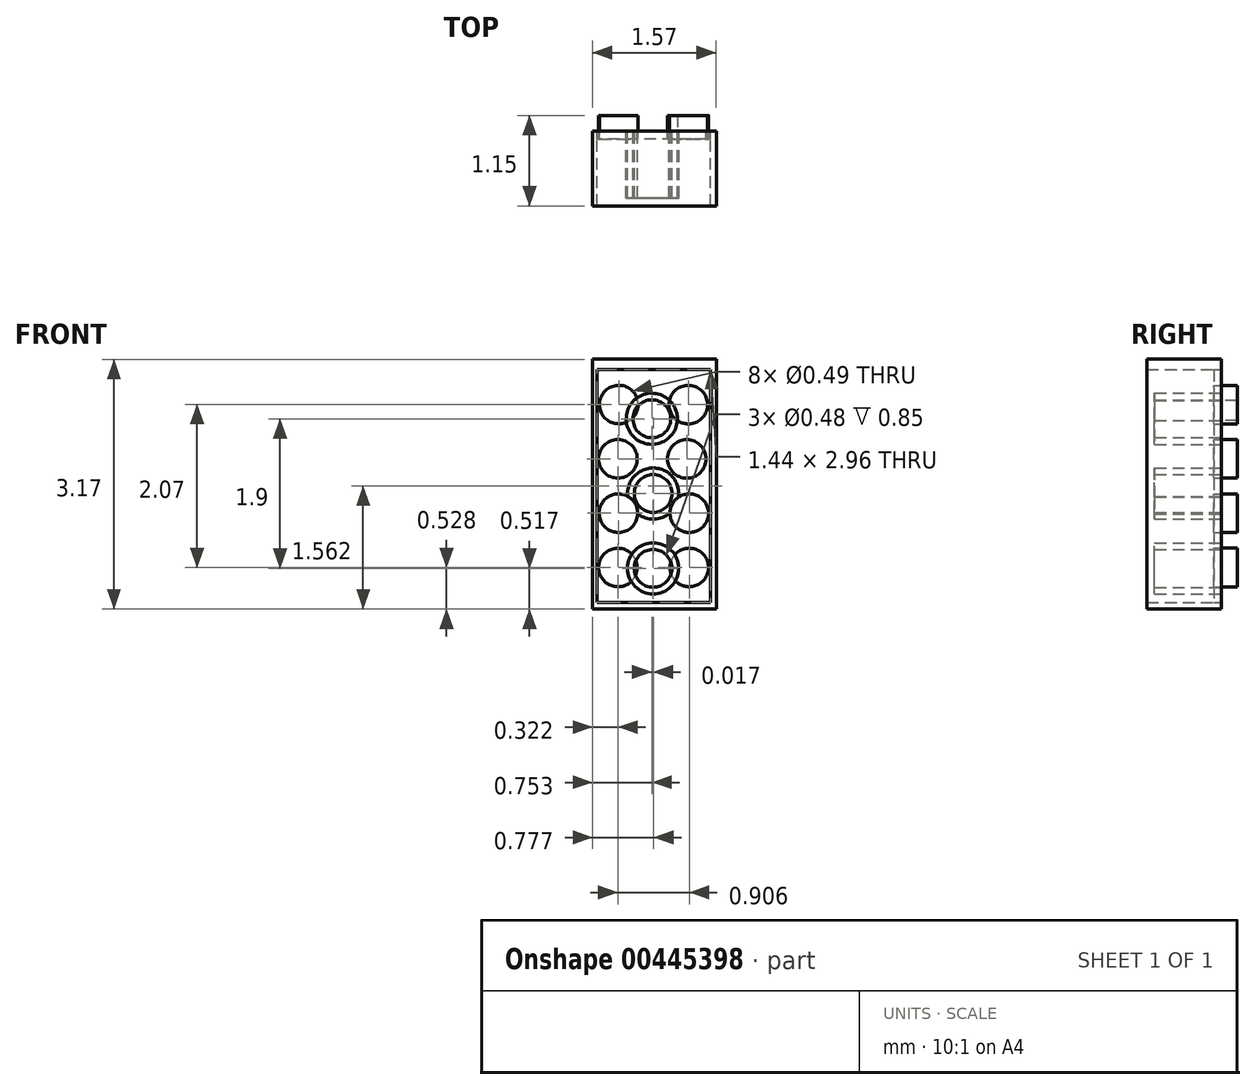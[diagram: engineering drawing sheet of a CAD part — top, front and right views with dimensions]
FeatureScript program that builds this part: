
annotation { "Feature Type Name" : "Feature", "Feature Type Description" : "" }
export const myFeature = defineFeature(function(context is Context, id is Id, definition is map)
    precondition{}
    {
        {
            var Q0;
            Q0=qCreatedBy(makeId("Front.planeOp"),FACE);
            var sketch = newSketch(context, id + "F0", { "sketchPlane" : qUnion([Q0])});
            skLineSegment(sketch, "E0.bottom", {"start": v(-2.81, -5.22) * mm, "end": v(-1.24, -5.22) * mm});
            skLineSegment(sketch, "E0.top", {"start": v(-2.81, -8.4) * mm, "end": v(-1.24, -8.4) * mm});
            skLineSegment(sketch, "E0.left", {"start": v(-2.81, -5.22) * mm, "end": v(-2.81, -8.4) * mm});
            skLineSegment(sketch, "E0.right", {"start": v(-1.24, -5.22) * mm, "end": v(-1.24, -8.4) * mm});
            skLineSegment(sketch, "E1", {"start": v(-2.75, -5.22) * mm, "end": v(-2.75, -8.4) * mm});
            skLineSegment(sketch, "E2", {"start": v(-2.75, -8.4) * mm, "end": v(-2.81, -8.3) * mm});
            skLineSegment(sketch, "E3", {"start": v(-2.81, -8.3) * mm, "end": v(-1.24, -8.3) * mm});
            skLineSegment(sketch, "E4", {"start": v(-1.24, -8.3) * mm, "end": v(-1.31, -8.4) * mm});
            skLineSegment(sketch, "E5", {"start": v(-1.31, -8.4) * mm, "end": v(-1.31, -5.22) * mm});
            skLineSegment(sketch, "E6", {"start": v(-1.31, -5.22) * mm, "end": v(-1.24, -5.35) * mm});
            skLineSegment(sketch, "E7", {"start": v(-1.24, -5.35) * mm, "end": v(-2.81, -5.35) * mm});
            skCircle(sketch, "E8", {"center": v(-2.48, -5.8) * mm, "radius": 0.24 * mm});
            skCircle(sketch, "E9", {"center": v(-1.6, -5.8) * mm, "radius": 0.24 * mm});
            skCircle(sketch, "E10", {"center": v(-2.49, -6.48) * mm, "radius": 0.24 * mm});
            skCircle(sketch, "E11", {"center": v(-1.61, -6.48) * mm, "radius": 0.24 * mm});
            skCircle(sketch, "E12", {"center": v(-2.48, -7.17) * mm, "radius": 0.24 * mm});
            skCircle(sketch, "E13", {"center": v(-1.58, -7.17) * mm, "radius": 0.24 * mm});
            skCircle(sketch, "E14", {"center": v(-1.58, -7.86) * mm, "radius": 0.24 * mm});
            skCircle(sketch, "E15", {"center": v(-2.49, -7.86) * mm, "radius": 0.24 * mm});
            skSolve(sketch);
        }
        {
            var Q0;
            Q0=makeQuery(id+"F0.imprint","IMPRINT",FACE,{"disambiguationData":[TD([[makeQuery(id+"F0.imprint","IMPRINT",EDGE,{"derivedFrom":sQuery(id+"F0.wireOp",EDGE,"E8")}),-1.0]])]});
            var sketch = newSketch(context, id + "F1", { "sketchPlane" : qUnion([Q0])});
            skCircle(sketch, "E16", {"center": v(-2.06, -5.97) * mm, "radius": 0.33 * mm});
            skCircle(sketch, "E17", {"center": v(-2.04, -6.92) * mm, "radius": 0.33 * mm});
            skCircle(sketch, "E18", {"center": v(-2.04, -7.87) * mm, "radius": 0.33 * mm});
            skCircle(sketch, "E19", {"center": v(-2.06, -5.97) * mm, "radius": 0.24 * mm});
            skCircle(sketch, "E20", {"center": v(-2.04, -6.92) * mm, "radius": 0.24 * mm});
            skCircle(sketch, "E21", {"center": v(-2.04, -7.87) * mm, "radius": 0.24 * mm});
            skSolve(sketch);
        }
        {
            var Q0;
            {var subQ0=sQuery(id+"F0.wireOp",EDGE,"E1");var subQ1=sQuery(id+"F0.wireOp",EDGE,"E0.bottom");var subQ2=makeQuery(id+"F0.imprint","INTERSECT",VERTEX,{"derivedFrom":[subQ1,subQ0]});Q0=makeQuery(id+"F0.imprint","IMPRINT",FACE,{"disambiguationData":[TD([[makeQuery(id+"F0.imprint","IMPRINT",EDGE,{"disambiguationData":[TD([[subQ2,-1.0]])],"derivedFrom":subQ0}),1.0]])]});}
            var Q1;
            {var subQ0=sQuery(id+"F0.wireOp",EDGE,"E0.left");var subQ1=sQuery(id+"F0.wireOp",EDGE,"E0.bottom");var subQ2=makeQuery(id+"F0.imprint","INTERSECT",VERTEX,{"derivedFrom":[subQ1,subQ0]});Q1=makeQuery(id+"F0.imprint","IMPRINT",FACE,{"disambiguationData":[TD([[makeQuery(id+"F0.imprint","IMPRINT",EDGE,{"disambiguationData":[TD([[subQ2,-1.0]])],"derivedFrom":subQ1}),-1.0]])]});}
            var Q2;
            {var subQ3=sQuery(id+"F0.wireOp",EDGE,"E6");Q2=makeQuery(id+"F0.imprint","IMPRINT",FACE,{"disambiguationData":[TD([[makeQuery(id+"F0.imprint","IMPRINT",EDGE,{"derivedFrom":subQ3}),1.0]])]});}
            var Q3;
            {var subQ0=sQuery(id+"F0.wireOp",EDGE,"E6");Q3=makeQuery(id+"F0.imprint","IMPRINT",FACE,{"disambiguationData":[TD([[makeQuery(id+"F0.imprint","IMPRINT",EDGE,{"derivedFrom":subQ0}),-1.0]])]});}
            var Q4;
            {var subQ3=sQuery(id+"F0.wireOp",EDGE,"E4");Q4=makeQuery(id+"F0.imprint","IMPRINT",FACE,{"disambiguationData":[TD([[makeQuery(id+"F0.imprint","IMPRINT",EDGE,{"derivedFrom":subQ3}),1.0]])]});}
            var Q5;
            {var subQ0=sQuery(id+"F0.wireOp",EDGE,"E4");Q5=makeQuery(id+"F0.imprint","IMPRINT",FACE,{"disambiguationData":[TD([[makeQuery(id+"F0.imprint","IMPRINT",EDGE,{"derivedFrom":subQ0}),-1.0]])]});}
            var Q6;
            {var subQ3=sQuery(id+"F0.wireOp",EDGE,"E2");Q6=makeQuery(id+"F0.imprint","IMPRINT",FACE,{"disambiguationData":[TD([[makeQuery(id+"F0.imprint","IMPRINT",EDGE,{"derivedFrom":subQ3}),1.0]])]});}
            var Q7;
            {var subQ0=sQuery(id+"F0.wireOp",EDGE,"E1");var subQ5=sQuery(id+"F0.wireOp",EDGE,"E3");var subQ6=makeQuery(id+"F0.imprint","INTERSECT",VERTEX,{"derivedFrom":[subQ0,subQ5]});Q7=makeQuery(id+"F0.imprint","IMPRINT",FACE,{"disambiguationData":[TD([[makeQuery(id+"F0.imprint","IMPRINT",EDGE,{"disambiguationData":[TD([[subQ6,-1.0]])],"derivedFrom":subQ5}),-1.0]])]});}
            var Q8;
            {var subQ0=sQuery(id+"F0.wireOp",EDGE,"E2");Q8=makeQuery(id+"F0.imprint","IMPRINT",FACE,{"disambiguationData":[TD([[makeQuery(id+"F0.imprint","IMPRINT",EDGE,{"derivedFrom":subQ0}),-1.0]])]});}
            var Q9;
            {var subQ3=sQuery(id+"F0.wireOp",EDGE,"E7");var subQ5=sQuery(id+"F0.wireOp",EDGE,"E1");var subQ6=makeQuery(id+"F0.imprint","INTERSECT",VERTEX,{"derivedFrom":[subQ5,subQ3]});Q9=makeQuery(id+"F0.imprint","IMPRINT",FACE,{"disambiguationData":[TD([[makeQuery(id+"F0.imprint","IMPRINT",EDGE,{"disambiguationData":[TD([[subQ6,-1.0]])],"derivedFrom":subQ5}),-1.0]])]});}
            var Q10;
            {var subQ0=sQuery(id+"F0.wireOp",EDGE,"E3");var subQ5=sQuery(id+"F0.wireOp",EDGE,"E5");var subQ6=makeQuery(id+"F0.imprint","INTERSECT",VERTEX,{"derivedFrom":[subQ0,subQ5]});Q10=makeQuery(id+"F0.imprint","IMPRINT",FACE,{"disambiguationData":[TD([[makeQuery(id+"F0.imprint","IMPRINT",EDGE,{"disambiguationData":[TD([[subQ6,-1.0]])],"derivedFrom":subQ5}),-1.0]])]});}
            extrude(context, id + "F2", {"entities" : qUnion([Q0, Q1, Q2, Q3, Q4, Q5, Q6, Q7, Q8, Q9, Q10]), "depth" : 0.95 * mm});
        }
        {
            var Q0;
            Q0=makeQuery(id+"F0.imprint","IMPRINT",FACE,{"disambiguationData":[TD([[makeQuery(id+"F0.imprint","IMPRINT",EDGE,{"derivedFrom":sQuery(id+"F0.wireOp",EDGE,"E8")}),-1.0]])]});
            extrude(context, id + "F3", {"entities" : qUnion([Q0]), "depth" : 0.1 * mm});
        }
        {
            var Q0;
            Q0=makeQuery(id+"F0.imprint","IMPRINT",FACE,{"disambiguationData":[TD([[makeQuery(id+"F0.imprint","IMPRINT",EDGE,{"derivedFrom":sQuery(id+"F0.wireOp",EDGE,"E14")}),1.0]])]});
            var Q1;
            Q1=makeQuery(id+"F0.imprint","IMPRINT",FACE,{"disambiguationData":[TD([[makeQuery(id+"F0.imprint","IMPRINT",EDGE,{"derivedFrom":sQuery(id+"F0.wireOp",EDGE,"E15")}),1.0]])]});
            var Q2;
            Q2=makeQuery(id+"F0.imprint","IMPRINT",FACE,{"disambiguationData":[TD([[makeQuery(id+"F0.imprint","IMPRINT",EDGE,{"derivedFrom":sQuery(id+"F0.wireOp",EDGE,"E12")}),1.0]])]});
            var Q3;
            Q3=makeQuery(id+"F0.imprint","IMPRINT",FACE,{"disambiguationData":[TD([[makeQuery(id+"F0.imprint","IMPRINT",EDGE,{"derivedFrom":sQuery(id+"F0.wireOp",EDGE,"E13")}),1.0]])]});
            var Q4;
            Q4=makeQuery(id+"F0.imprint","IMPRINT",FACE,{"disambiguationData":[TD([[makeQuery(id+"F0.imprint","IMPRINT",EDGE,{"derivedFrom":sQuery(id+"F0.wireOp",EDGE,"E11")}),1.0]])]});
            var Q5;
            Q5=makeQuery(id+"F0.imprint","IMPRINT",FACE,{"disambiguationData":[TD([[makeQuery(id+"F0.imprint","IMPRINT",EDGE,{"derivedFrom":sQuery(id+"F0.wireOp",EDGE,"E10")}),1.0]])]});
            var Q6;
            Q6=makeQuery(id+"F0.imprint","IMPRINT",FACE,{"disambiguationData":[TD([[makeQuery(id+"F0.imprint","IMPRINT",EDGE,{"derivedFrom":sQuery(id+"F0.wireOp",EDGE,"E8")}),1.0]])]});
            var Q7;
            {var subQ0=sQuery(id+"F1.wireOp",EDGE,"E16");var subQ1=makeQuery(id+"F0.imprint","IMPRINT",EDGE,{"derivedFrom":sQuery(id+"F0.wireOp",EDGE,"E9")});var subQ2=makeQuery(id+"F1.imprint","INTERSECT",VERTEX,{"disambiguationData":[OD(0.0)],"derivedFrom":[subQ1,subQ0]});Q7=makeQuery(id+"F1.imprint","IMPRINT",FACE,{"disambiguationData":[TD([[makeQuery(id+"F1.imprint","IMPRINT",EDGE,{"disambiguationData":[TD([[subQ2,1.0]])],"derivedFrom":subQ0}),-1.0]])]});}
            var Q8;
            Q8=makeQuery(id+"F0.imprint","IMPRINT",FACE,{"disambiguationData":[TD([[makeQuery(id+"F0.imprint","IMPRINT",EDGE,{"derivedFrom":sQuery(id+"F0.wireOp",EDGE,"E9")}),1.0]])]});
            extrude(context, id + "F4", {"entities" : qUnion([Q0, Q1, Q2, Q3, Q4, Q5, Q6, Q7, Q8]), "oppositeDirection" : true, "depth" : 0.2 * mm});
        }
        {
            var Q0;
            {var subQ0=sQuery(id+"F1.wireOp",EDGE,"E18");var subQ1=makeQuery(id+"F0.imprint","IMPRINT",EDGE,{"derivedFrom":sQuery(id+"F0.wireOp",EDGE,"E15")});var subQ2=makeQuery(id+"F1.imprint","INTERSECT",VERTEX,{"disambiguationData":[OD(1.0)],"derivedFrom":[subQ1,subQ0]});Q0=makeQuery(id+"F1.imprint","IMPRINT",FACE,{"disambiguationData":[TD([[makeQuery(id+"F1.imprint","IMPRINT",EDGE,{"disambiguationData":[TD([[subQ2,-1.0]])],"derivedFrom":subQ0}),1.0]])]});}
            var Q1;
            {var subQ0=sQuery(id+"F1.wireOp",EDGE,"E18");var subQ1=makeQuery(id+"F0.imprint","IMPRINT",EDGE,{"derivedFrom":sQuery(id+"F0.wireOp",EDGE,"E15")});var subQ2=makeQuery(id+"F1.imprint","INTERSECT",VERTEX,{"disambiguationData":[OD(0.0)],"derivedFrom":[subQ1,subQ0]});Q1=makeQuery(id+"F1.imprint","IMPRINT",FACE,{"disambiguationData":[TD([[makeQuery(id+"F1.imprint","IMPRINT",EDGE,{"disambiguationData":[TD([[subQ2,-1.0]])],"derivedFrom":subQ0}),1.0]])]});}
            var Q2;
            Q2=makeQuery(id+"F1.imprint","IMPRINT",FACE,{"disambiguationData":[TD([[makeQuery(id+"F1.imprint","IMPRINT",EDGE,{"derivedFrom":sQuery(id+"F1.wireOp",EDGE,"E20")}),-1.0]])]});
            var Q3;
            {var subQ0=sQuery(id+"F1.wireOp",EDGE,"E17");var subQ1=makeQuery(id+"F0.imprint","IMPRINT",EDGE,{"derivedFrom":sQuery(id+"F0.wireOp",EDGE,"E12")});var subQ2=makeQuery(id+"F1.imprint","INTERSECT",VERTEX,{"disambiguationData":[OD(0.0)],"derivedFrom":[subQ1,subQ0]});Q3=makeQuery(id+"F1.imprint","IMPRINT",FACE,{"disambiguationData":[TD([[makeQuery(id+"F1.imprint","IMPRINT",EDGE,{"disambiguationData":[TD([[subQ2,1.0]])],"derivedFrom":subQ0}),1.0]])]});}
            var Q4;
            {var subQ0=sQuery(id+"F1.wireOp",EDGE,"E17");var subQ1=makeQuery(id+"F0.imprint","IMPRINT",EDGE,{"derivedFrom":sQuery(id+"F0.wireOp",EDGE,"E13")});var subQ2=makeQuery(id+"F1.imprint","INTERSECT",VERTEX,{"disambiguationData":[OD(0.0)],"derivedFrom":[subQ1,subQ0]});Q4=makeQuery(id+"F1.imprint","IMPRINT",FACE,{"disambiguationData":[TD([[makeQuery(id+"F1.imprint","IMPRINT",EDGE,{"disambiguationData":[TD([[subQ2,-1.0]])],"derivedFrom":subQ0}),1.0]])]});}
            var Q5;
            {var subQ0=sQuery(id+"F1.wireOp",EDGE,"E16");var subQ1=makeQuery(id+"F0.imprint","IMPRINT",EDGE,{"derivedFrom":sQuery(id+"F0.wireOp",EDGE,"E8")});var subQ2=makeQuery(id+"F1.imprint","INTERSECT",VERTEX,{"disambiguationData":[OD(0.0)],"derivedFrom":[subQ1,subQ0]});Q5=makeQuery(id+"F1.imprint","IMPRINT",FACE,{"disambiguationData":[TD([[makeQuery(id+"F1.imprint","IMPRINT",EDGE,{"disambiguationData":[TD([[subQ2,1.0]])],"derivedFrom":subQ0}),1.0]])]});}
            var Q6;
            {var subQ0=sQuery(id+"F1.wireOp",EDGE,"E16");var subQ1=makeQuery(id+"F0.imprint","IMPRINT",EDGE,{"derivedFrom":sQuery(id+"F0.wireOp",EDGE,"E8")});var subQ2=makeQuery(id+"F1.imprint","INTERSECT",VERTEX,{"disambiguationData":[OD(0.0)],"derivedFrom":[subQ1,subQ0]});Q6=makeQuery(id+"F1.imprint","IMPRINT",FACE,{"disambiguationData":[TD([[makeQuery(id+"F1.imprint","IMPRINT",EDGE,{"disambiguationData":[TD([[subQ2,-1.0]])],"derivedFrom":subQ0}),1.0]])]});}
            var Q7;
            {var subQ0=sQuery(id+"F1.wireOp",EDGE,"E18");var subQ1=makeQuery(id+"F0.imprint","IMPRINT",EDGE,{"derivedFrom":sQuery(id+"F0.wireOp",EDGE,"E15")});var subQ2=makeQuery(id+"F1.imprint","INTERSECT",VERTEX,{"disambiguationData":[OD(0.0)],"derivedFrom":[subQ1,subQ0]});Q7=makeQuery(id+"F1.imprint","IMPRINT",FACE,{"disambiguationData":[TD([[makeQuery(id+"F1.imprint","IMPRINT",EDGE,{"disambiguationData":[TD([[subQ2,1.0]])],"derivedFrom":subQ0}),1.0]])]});}
            var Q8;
            {var subQ0=sQuery(id+"F1.wireOp",EDGE,"E18");var subQ1=makeQuery(id+"F0.imprint","IMPRINT",EDGE,{"derivedFrom":sQuery(id+"F0.wireOp",EDGE,"E14")});var subQ2=makeQuery(id+"F1.imprint","INTERSECT",VERTEX,{"disambiguationData":[OD(0.0)],"derivedFrom":[subQ1,subQ0]});Q8=makeQuery(id+"F1.imprint","IMPRINT",FACE,{"disambiguationData":[TD([[makeQuery(id+"F1.imprint","IMPRINT",EDGE,{"disambiguationData":[TD([[subQ2,1.0]])],"derivedFrom":subQ0}),1.0]])]});}
            extrude(context, id + "F5", {"entities" : qUnion([Q0, Q1, Q2, Q3, Q4, Q5, Q6, Q7, Q8]), "depth" : 0.85 * mm});
        }
    });
